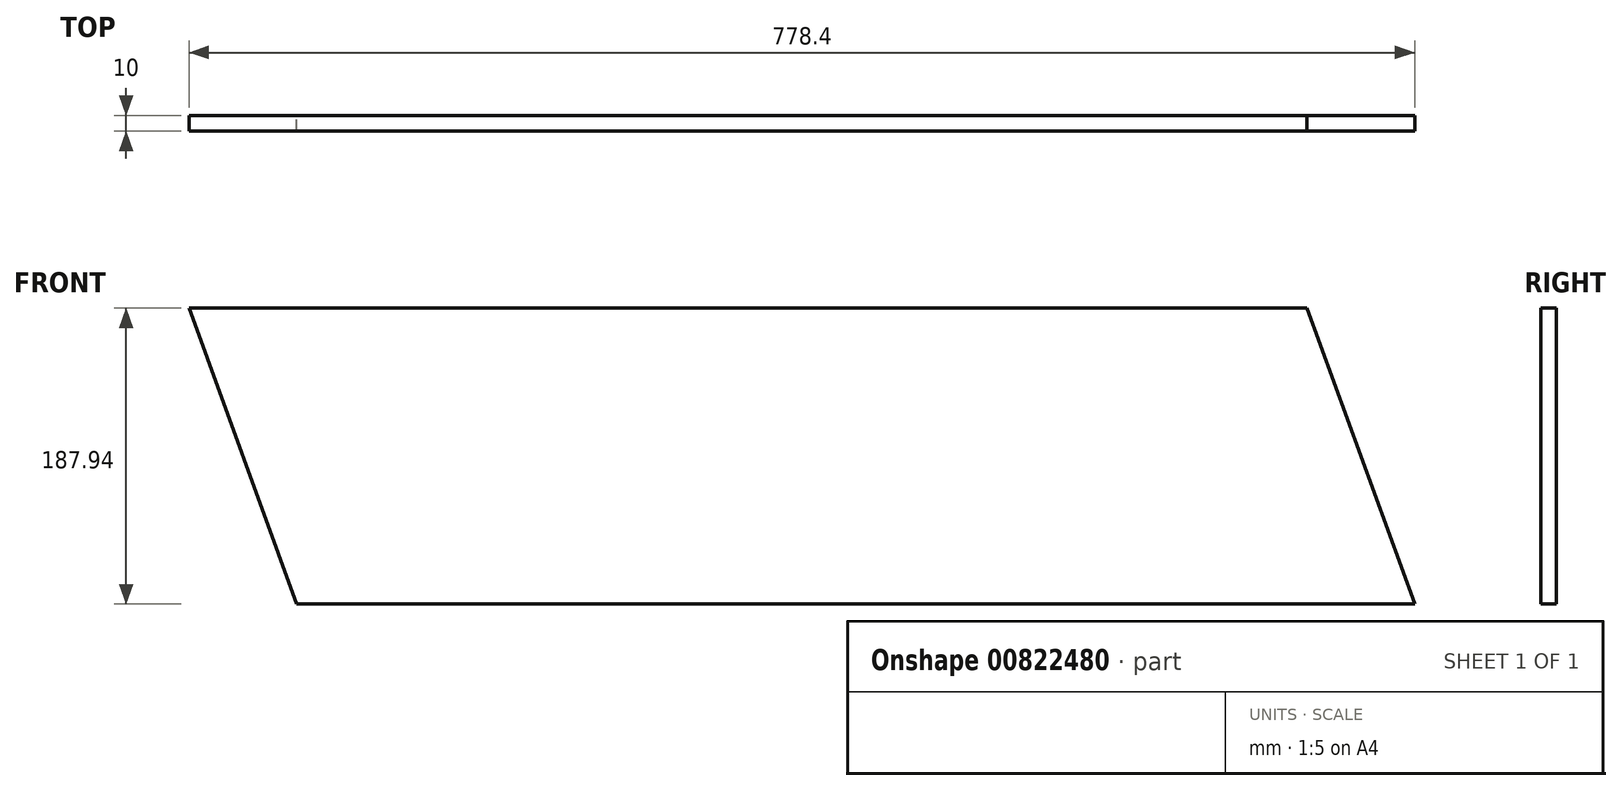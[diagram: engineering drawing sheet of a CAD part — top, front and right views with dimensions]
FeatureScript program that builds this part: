
annotation { "Feature Type Name" : "Feature", "Feature Type Description" : "" }
export const myFeature = defineFeature(function(context is Context, id is Id, definition is map)
    precondition{}
    {
        {
            var Q0;
            Q0=qCreatedBy(makeId("Front.planeOp"),FACE);
            var sketch = newSketch(context, id + "F0", { "sketchPlane" : qUnion([Q0])});
            skLineSegment(sketch, "E0", {"start": v(-270.49, -412.79) * mm, "end": v(439.51, -412.79) * mm});
            skLineSegment(sketch, "E1", {"start": v(-338.89, -224.85) * mm, "end": v(-270.49, -412.79) * mm});
            skLineSegment(sketch, "E2", {"start": v(371.11, -224.85) * mm, "end": v(439.51, -412.79) * mm});
            skLineSegment(sketch, "E3", {"start": v(-338.89, -224.85) * mm, "end": v(371.11, -224.85) * mm});
            skSolve(sketch);
        }
        {
            var Q0;
            Q0=makeQuery(id+"F0.imprint","IMPRINT",FACE,{"disambiguationData":[TD([[makeQuery(id+"F0.imprint","IMPRINT",EDGE,{"derivedFrom":sQuery(id+"F0.wireOp",EDGE,"E0")}),1.0]])]});
            var Q1;
            Q1=makeQuery(id+"F0.imprint","IMPRINT",FACE,{"disambiguationData":[TD([[makeQuery(id+"F0.imprint","IMPRINT",EDGE,{"derivedFrom":sQuery(id+"F0.wireOp",EDGE,"pgvErVKm-BDVy-IWiA-WicW-B6g0RcLyOcZ5")}),1.0]])]});
            var Q2;
            Q2=makeQuery(id+"F0.imprint","IMPRINT",FACE,{"disambiguationData":[TD([[makeQuery(id+"F0.imprint","IMPRINT",EDGE,{"derivedFrom":sQuery(id+"F0.wireOp",EDGE,"eTA587d8-7fkE-qv8w-ftzY-MF9U7WKkl773")}),1.0]])]});
            extrude(context, id + "F1", {"entities" : qUnion([Q0, Q1, Q2]), "depth" : 10 * mm, "offsetDistance" : 25.4 * mm});
        }
    });
